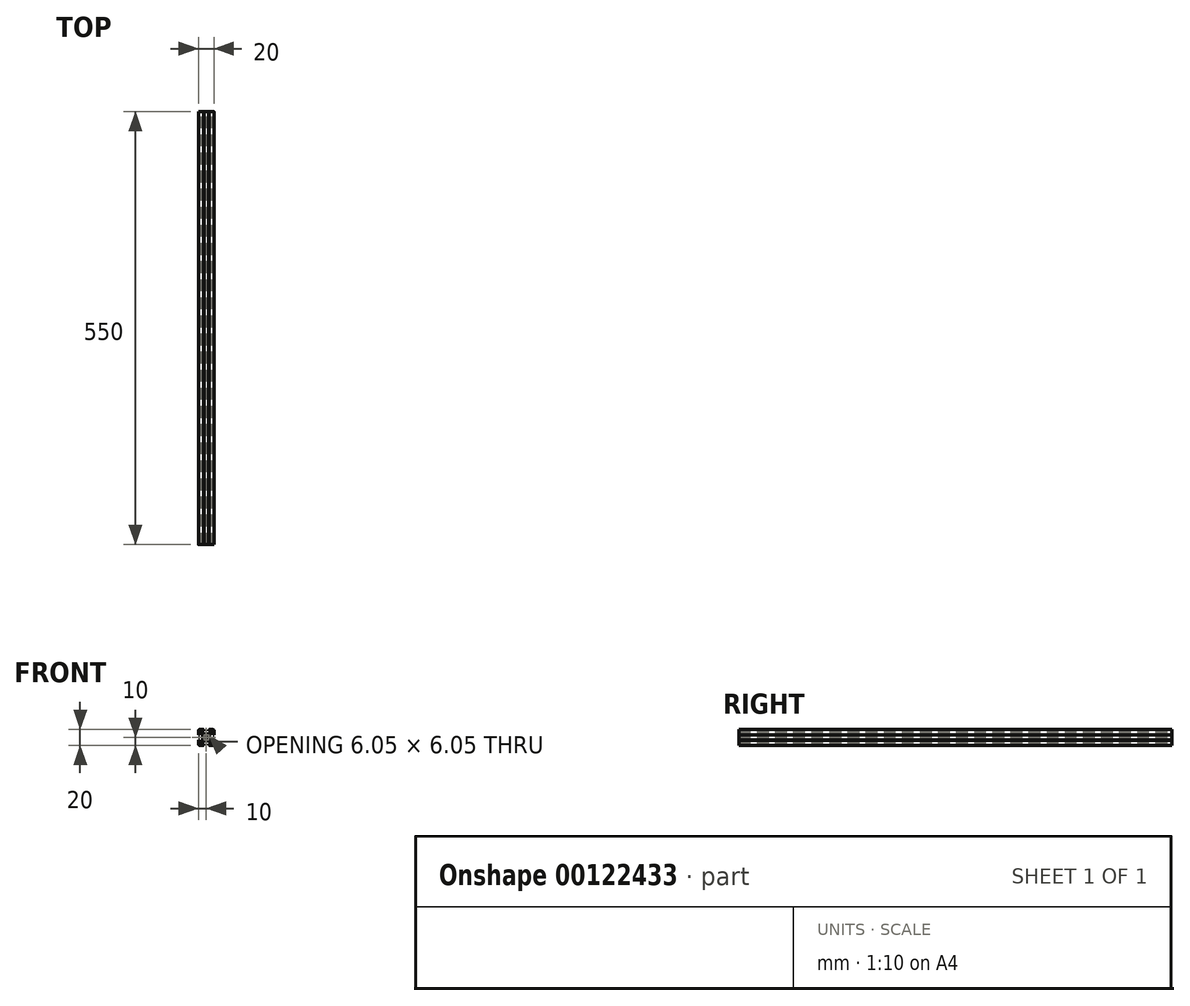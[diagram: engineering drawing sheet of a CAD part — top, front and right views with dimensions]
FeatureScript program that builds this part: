
annotation { "Feature Type Name" : "Feature", "Feature Type Description" : "" }
export const myFeature = defineFeature(function(context is Context, id is Id, definition is map)
    precondition{}
    {
        {
            var Q0;
            Q0=qCreatedBy(makeId("Front.planeOp"),FACE);
            var sketch = newSketch(context, id + "F0", { "sketchPlane" : qUnion([Q0])});
            skLineSegment(sketch, "E0", {"start": v(0, 4.5) * mm, "end": v(3.44, 4.5) * mm});
            skLineSegment(sketch, "E1", {"start": v(3.44, 4.5) * mm, "end": v(6, 7.06) * mm});
            skLineSegment(sketch, "E2", {"start": v(6, 7.06) * mm, "end": v(6, 8.5) * mm});
            skLineSegment(sketch, "E3", {"start": v(6, 8.5) * mm, "end": v(3, 8.5) * mm});
            skLineSegment(sketch, "E4", {"start": v(3, 8.5) * mm, "end": v(3, 9.5) * mm});
            skLineSegment(sketch, "E5", {"start": v(3, 9.5) * mm, "end": v(3.5, 9.5) * mm});
            skLineSegment(sketch, "E6", {"start": v(3.5, 9.5) * mm, "end": v(3.5, 10) * mm});
            skLineSegment(sketch, "E7", {"start": v(3.5, 10) * mm, "end": v(8.5, 10) * mm});
            skLineSegment(sketch, "E8", {"start": v(0, 0) * mm, "end": v(11.95, 11.95) * mm, "construction": true});
            skLineSegment(sketch, "E9.MirrorCS", {"start": v(9.5, 3) * mm, "end": v(9.5, 3.5) * mm});
            skLineSegment(sketch, "E10.MirrorCS", {"start": v(9.5, 3.5) * mm, "end": v(10, 3.5) * mm});
            skLineSegment(sketch, "E11.MirrorCS", {"start": v(4.5, 3.44) * mm, "end": v(7.06, 6) * mm});
            skLineSegment(sketch, "E12.MirrorCS", {"start": v(7.06, 6) * mm, "end": v(8.5, 6) * mm});
            skLineSegment(sketch, "E13.MirrorCS", {"start": v(8.5, 6) * mm, "end": v(8.5, 3) * mm});
            skLineSegment(sketch, "E14.MirrorCS", {"start": v(8.5, 3) * mm, "end": v(9.5, 3) * mm});
            skLineSegment(sketch, "E15.MirrorCS", {"start": v(10, 3.5) * mm, "end": v(10, 8.5) * mm});
            skLineSegment(sketch, "E16.MirrorCS", {"start": v(4.5, 0) * mm, "end": v(4.5, 3.44) * mm});
            skPoint(sketch, "E17.visualSharp", {"position": v(10, 10) * mm});
            skArc(sketch, "E17.filletArc", {"start": v(10, 8.5) * mm, "mid": v(9.56, 9.56) * mm, "end": v(8.5, 10) * mm});
            skArc(sketch, "E18", {"start": v(0, 2.75) * mm, "mid": v(0.7, 2.66) * mm, "end": v(1.34, 2.4) * mm});
            skLineSegment(sketch, "E19", {"start": v(1.34, 2.4) * mm, "end": v(1.96, 3.02) * mm});
            skLineSegment(sketch, "E20", {"start": v(1.96, 3.02) * mm, "end": v(3.02, 1.96) * mm});
            skLineSegment(sketch, "E21", {"start": v(3.02, 1.96) * mm, "end": v(2.4, 1.34) * mm});
            skArc(sketch, "E22.trimOffspring", {"start": v(2.4, 1.34) * mm, "mid": v(2.66, 0.7) * mm, "end": v(2.75, 0) * mm});
            skLineSegment(sketch, "E23.MirrorCS", {"start": v(1.96, 3.02) * mm, "end": v(1.34, 2.4) * mm});
            skLineSegment(sketch, "E24.MirrorCS", {"start": v(2.4, 1.34) * mm, "end": v(3.02, 1.96) * mm});
            skArc(sketch, "E25.MirrorCS", {"start": v(8.5, 10) * mm, "mid": v(9.56, 9.56) * mm, "end": v(10, 8.5) * mm});
            skArc(sketch, "E26.MirrorCS", {"start": v(2.75, 0) * mm, "mid": v(2.66, 0.7) * mm, "end": v(2.4, 1.34) * mm});
            skArc(sketch, "E27.MirrorCS", {"start": v(1.34, 2.4) * mm, "mid": v(0.7, 2.66) * mm, "end": v(0, 2.75) * mm});
            skLineSegment(sketch, "E28.MirrorCS", {"start": v(3.02, 1.96) * mm, "end": v(1.96, 3.02) * mm});
            skLineSegment(sketch, "E29.MirrorCS", {"start": v(3, -9.5) * mm, "end": v(3.5, -9.5) * mm});
            skLineSegment(sketch, "E30.MirrorCS", {"start": v(9.5, -3) * mm, "end": v(9.5, -3.5) * mm});
            skLineSegment(sketch, "E31.MirrorCS", {"start": v(9.5, -3.5) * mm, "end": v(10, -3.5) * mm});
            skLineSegment(sketch, "E32.MirrorCS", {"start": v(3.5, -9.5) * mm, "end": v(3.5, -10) * mm});
            skLineSegment(sketch, "E33.MirrorCS", {"start": v(6, -7.06) * mm, "end": v(6, -8.5) * mm});
            skArc(sketch, "E34.MirrorCS", {"start": v(8.5, -10) * mm, "mid": v(9.56, -9.56) * mm, "end": v(10, -8.5) * mm});
            skLineSegment(sketch, "E35.MirrorCS", {"start": v(3.5, -10) * mm, "end": v(8.5, -10) * mm});
            skLineSegment(sketch, "E36.MirrorCS", {"start": v(0, -4.5) * mm, "end": v(3.44, -4.5) * mm});
            skLineSegment(sketch, "E37.MirrorCS", {"start": v(3.02, -1.96) * mm, "end": v(1.96, -3.02) * mm});
            skLineSegment(sketch, "E38.MirrorCS", {"start": v(1.34, -2.4) * mm, "end": v(1.96, -3.02) * mm});
            skLineSegment(sketch, "E39.MirrorCS", {"start": v(4.5, -3.44) * mm, "end": v(7.06, -6) * mm});
            skLineSegment(sketch, "E40.MirrorCS", {"start": v(7.06, -6) * mm, "end": v(8.5, -6) * mm});
            skLineSegment(sketch, "E41.MirrorCS", {"start": v(3.44, -4.5) * mm, "end": v(6, -7.06) * mm});
            skLineSegment(sketch, "E42.MirrorCS", {"start": v(6, -8.5) * mm, "end": v(3, -8.5) * mm});
            skLineSegment(sketch, "E43.MirrorCS", {"start": v(8.5, -6) * mm, "end": v(8.5, -3) * mm});
            skLineSegment(sketch, "E44.MirrorCS", {"start": v(10, -3.5) * mm, "end": v(10, -8.5) * mm});
            skLineSegment(sketch, "E45.MirrorCS", {"start": v(8.5, -3) * mm, "end": v(9.5, -3) * mm});
            skLineSegment(sketch, "E46.MirrorCS", {"start": v(3.02, -1.96) * mm, "end": v(2.4, -1.34) * mm});
            skLineSegment(sketch, "E47.MirrorCS", {"start": v(4.5, 0) * mm, "end": v(4.5, -3.44) * mm});
            skLineSegment(sketch, "E48.MirrorCS", {"start": v(3, -8.5) * mm, "end": v(3, -9.5) * mm});
            skPoint(sketch, "E49.MirrorP", {"position": v(10, -10) * mm});
            skLineSegment(sketch, "E50.MirrorCS", {"start": v(1.96, -3.02) * mm, "end": v(3.02, -1.96) * mm});
            skLineSegment(sketch, "E51.MirrorCS", {"start": v(1.96, -3.02) * mm, "end": v(1.34, -2.4) * mm});
            skArc(sketch, "E52.MirrorCS", {"start": v(10, -8.5) * mm, "mid": v(9.56, -9.56) * mm, "end": v(8.5, -10) * mm});
            skArc(sketch, "E53.MirrorCS", {"start": v(0, -2.75) * mm, "mid": v(0.7, -2.66) * mm, "end": v(1.34, -2.4) * mm});
            skArc(sketch, "E54.MirrorCS", {"start": v(2.75, 0) * mm, "mid": v(2.66, -0.7) * mm, "end": v(2.4, -1.34) * mm});
            skArc(sketch, "E55.MirrorCS", {"start": v(2.4, -1.34) * mm, "mid": v(2.66, -0.7) * mm, "end": v(2.75, 0) * mm});
            skLineSegment(sketch, "E56.MirrorCS", {"start": v(2.4, -1.34) * mm, "end": v(3.02, -1.96) * mm});
            skArc(sketch, "E57.MirrorCS", {"start": v(1.34, -2.4) * mm, "mid": v(0.7, -2.66) * mm, "end": v(0, -2.75) * mm});
            skLineSegment(sketch, "E58.MirrorCS", {"start": v(-1.34, 2.4) * mm, "end": v(-1.96, 3.02) * mm});
            skLineSegment(sketch, "E59.MirrorCS", {"start": v(-9.5, 3) * mm, "end": v(-9.5, 3.5) * mm});
            skLineSegment(sketch, "E60.MirrorCS", {"start": v(-9.5, -3) * mm, "end": v(-9.5, -3.5) * mm});
            skLineSegment(sketch, "E61.MirrorCS", {"start": v(-3.02, 1.96) * mm, "end": v(-2.4, 1.34) * mm});
            skLineSegment(sketch, "E62.MirrorCS", {"start": v(-3.5, 9.5) * mm, "end": v(-3.5, 10) * mm});
            skLineSegment(sketch, "E63.MirrorCS", {"start": v(-3, -9.5) * mm, "end": v(-3.5, -9.5) * mm});
            skLineSegment(sketch, "E64.MirrorCS", {"start": v(-1.34, -2.4) * mm, "end": v(-1.96, -3.02) * mm});
            skLineSegment(sketch, "E65.MirrorCS", {"start": v(-3, 9.5) * mm, "end": v(-3.5, 9.5) * mm});
            skLineSegment(sketch, "E66.MirrorCS", {"start": v(-9.5, -3.5) * mm, "end": v(-10, -3.5) * mm});
            skLineSegment(sketch, "E67.MirrorCS", {"start": v(-9.5, 3.5) * mm, "end": v(-10, 3.5) * mm});
            skLineSegment(sketch, "E68.MirrorCS", {"start": v(-3.02, -1.96) * mm, "end": v(-2.4, -1.34) * mm});
            skLineSegment(sketch, "E69.MirrorCS", {"start": v(-3.5, -9.5) * mm, "end": v(-3.5, -10) * mm});
            skLineSegment(sketch, "E70.MirrorCS", {"start": v(-1.96, -3.02) * mm, "end": v(-1.34, -2.4) * mm});
            skLineSegment(sketch, "E71.MirrorCS", {"start": v(-2.4, -1.34) * mm, "end": v(-3.02, -1.96) * mm});
            skLineSegment(sketch, "E72.MirrorCS", {"start": v(-1.96, 3.02) * mm, "end": v(-1.34, 2.4) * mm});
            skLineSegment(sketch, "E73.MirrorCS", {"start": v(-2.4, 1.34) * mm, "end": v(-3.02, 1.96) * mm});
            skLineSegment(sketch, "E74.MirrorCS", {"start": v(-3.5, 10) * mm, "end": v(-8.5, 10) * mm});
            skLineSegment(sketch, "E75.MirrorCS", {"start": v(-8.5, 6) * mm, "end": v(-8.5, 3) * mm});
            skLineSegment(sketch, "E76.MirrorCS", {"start": v(-6, 8.5) * mm, "end": v(-3, 8.5) * mm});
            skLineSegment(sketch, "E77.MirrorCS", {"start": v(-3, 8.5) * mm, "end": v(-3, 9.5) * mm});
            skLineSegment(sketch, "E78.MirrorCS", {"start": v(-3.5, -10) * mm, "end": v(-8.5, -10) * mm});
            skLineSegment(sketch, "E79.MirrorCS", {"start": v(-6, 7.06) * mm, "end": v(-6, 8.5) * mm});
            skLineSegment(sketch, "E80.MirrorCS", {"start": v(-3, -8.5) * mm, "end": v(-3, -9.5) * mm});
            skPoint(sketch, "E81.MirrorP", {"position": v(-10, -10) * mm});
            skLineSegment(sketch, "E82.MirrorCS", {"start": v(-4.5, 3.44) * mm, "end": v(-7.06, 6) * mm});
            skLineSegment(sketch, "E83.MirrorCS", {"start": v(-7.06, 6) * mm, "end": v(-8.5, 6) * mm});
            skLineSegment(sketch, "E84.MirrorCS", {"start": v(-3.44, 4.5) * mm, "end": v(-6, 7.06) * mm});
            skLineSegment(sketch, "E85.MirrorCS", {"start": v(-10, -3.5) * mm, "end": v(-10, -8.5) * mm});
            skLineSegment(sketch, "E86.MirrorCS", {"start": v(-7.06, -6) * mm, "end": v(-8.5, -6) * mm});
            skLineSegment(sketch, "E87.MirrorCS", {"start": v(-8.5, -6) * mm, "end": v(-8.5, -3) * mm});
            skLineSegment(sketch, "E88.MirrorCS", {"start": v(-4.5, 0) * mm, "end": v(-4.5, -3.44) * mm});
            skLineSegment(sketch, "E89.MirrorCS", {"start": v(-4.5, -3.44) * mm, "end": v(-7.06, -6) * mm});
            skLineSegment(sketch, "E90.MirrorCS", {"start": v(-1.96, 3.02) * mm, "end": v(-3.02, 1.96) * mm});
            skLineSegment(sketch, "E91.MirrorCS", {"start": v(-4.5, 0) * mm, "end": v(-4.5, 3.44) * mm});
            skLineSegment(sketch, "E92.MirrorCS", {"start": v(0, -4.5) * mm, "end": v(-3.44, -4.5) * mm});
            skLineSegment(sketch, "E93.MirrorCS", {"start": v(-6, -7.06) * mm, "end": v(-6, -8.5) * mm});
            skArc(sketch, "E94.MirrorCS", {"start": v(-8.5, 10) * mm, "mid": v(-9.56, 9.56) * mm, "end": v(-10, 8.5) * mm});
            skLineSegment(sketch, "E95.MirrorCS", {"start": v(-10, 3.5) * mm, "end": v(-10, 8.5) * mm});
            skPoint(sketch, "E96.MirrorP", {"position": v(-10, 10) * mm});
            skLineSegment(sketch, "E97.MirrorCS", {"start": v(-6, -8.5) * mm, "end": v(-3, -8.5) * mm});
            skArc(sketch, "E98.MirrorCS", {"start": v(-8.5, -10) * mm, "mid": v(-9.56, -9.56) * mm, "end": v(-10, -8.5) * mm});
            skLineSegment(sketch, "E99.MirrorCS", {"start": v(0, 4.5) * mm, "end": v(-3.44, 4.5) * mm});
            skLineSegment(sketch, "E100.MirrorCS", {"start": v(-8.5, 3) * mm, "end": v(-9.5, 3) * mm});
            skLineSegment(sketch, "E101.MirrorCS", {"start": v(-1.96, -3.02) * mm, "end": v(-3.02, -1.96) * mm});
            skLineSegment(sketch, "E102.MirrorCS", {"start": v(-8.5, -3) * mm, "end": v(-9.5, -3) * mm});
            skLineSegment(sketch, "E103.MirrorCS", {"start": v(-3.44, -4.5) * mm, "end": v(-6, -7.06) * mm});
            skLineSegment(sketch, "E104.MirrorCS", {"start": v(-3.02, -1.96) * mm, "end": v(-1.96, -3.02) * mm});
            skArc(sketch, "E105.MirrorCS", {"start": v(-10, 8.5) * mm, "mid": v(-9.56, 9.56) * mm, "end": v(-8.5, 10) * mm});
            skArc(sketch, "E106.MirrorCS", {"start": v(-10, -8.5) * mm, "mid": v(-9.56, -9.56) * mm, "end": v(-8.5, -10) * mm});
            skLineSegment(sketch, "E107.MirrorCS", {"start": v(-3.02, 1.96) * mm, "end": v(-1.96, 3.02) * mm});
            skArc(sketch, "E108.MirrorCS", {"start": v(0, -2.75) * mm, "mid": v(-0.7, -2.66) * mm, "end": v(-1.34, -2.4) * mm});
            skArc(sketch, "E109.MirrorCS", {"start": v(-1.34, -2.4) * mm, "mid": v(-0.7, -2.66) * mm, "end": v(0, -2.75) * mm});
            skArc(sketch, "E110.MirrorCS", {"start": v(0, 2.75) * mm, "mid": v(-0.7, 2.66) * mm, "end": v(-1.34, 2.4) * mm});
            skArc(sketch, "E111.MirrorCS", {"start": v(-2.75, 0) * mm, "mid": v(-2.66, -0.7) * mm, "end": v(-2.4, -1.34) * mm});
            skArc(sketch, "E112.MirrorCS", {"start": v(-2.75, 0) * mm, "mid": v(-2.66, 0.7) * mm, "end": v(-2.4, 1.34) * mm});
            skArc(sketch, "E113.MirrorCS", {"start": v(-2.4, 1.34) * mm, "mid": v(-2.66, 0.7) * mm, "end": v(-2.75, 0) * mm});
            skArc(sketch, "E114.MirrorCS", {"start": v(-1.34, 2.4) * mm, "mid": v(-0.7, 2.66) * mm, "end": v(0, 2.75) * mm});
            skArc(sketch, "E115.MirrorCS", {"start": v(-2.4, -1.34) * mm, "mid": v(-2.66, -0.7) * mm, "end": v(-2.75, 0) * mm});
            skSolve(sketch);
        }
        {
            var Q0;
            Q0 = qSketchRegion(id + "F0", true);
            extrude(context, id + "F1", {"entities" : qUnion([Q0]), "depth" : 550 * mm});
        }
    });
